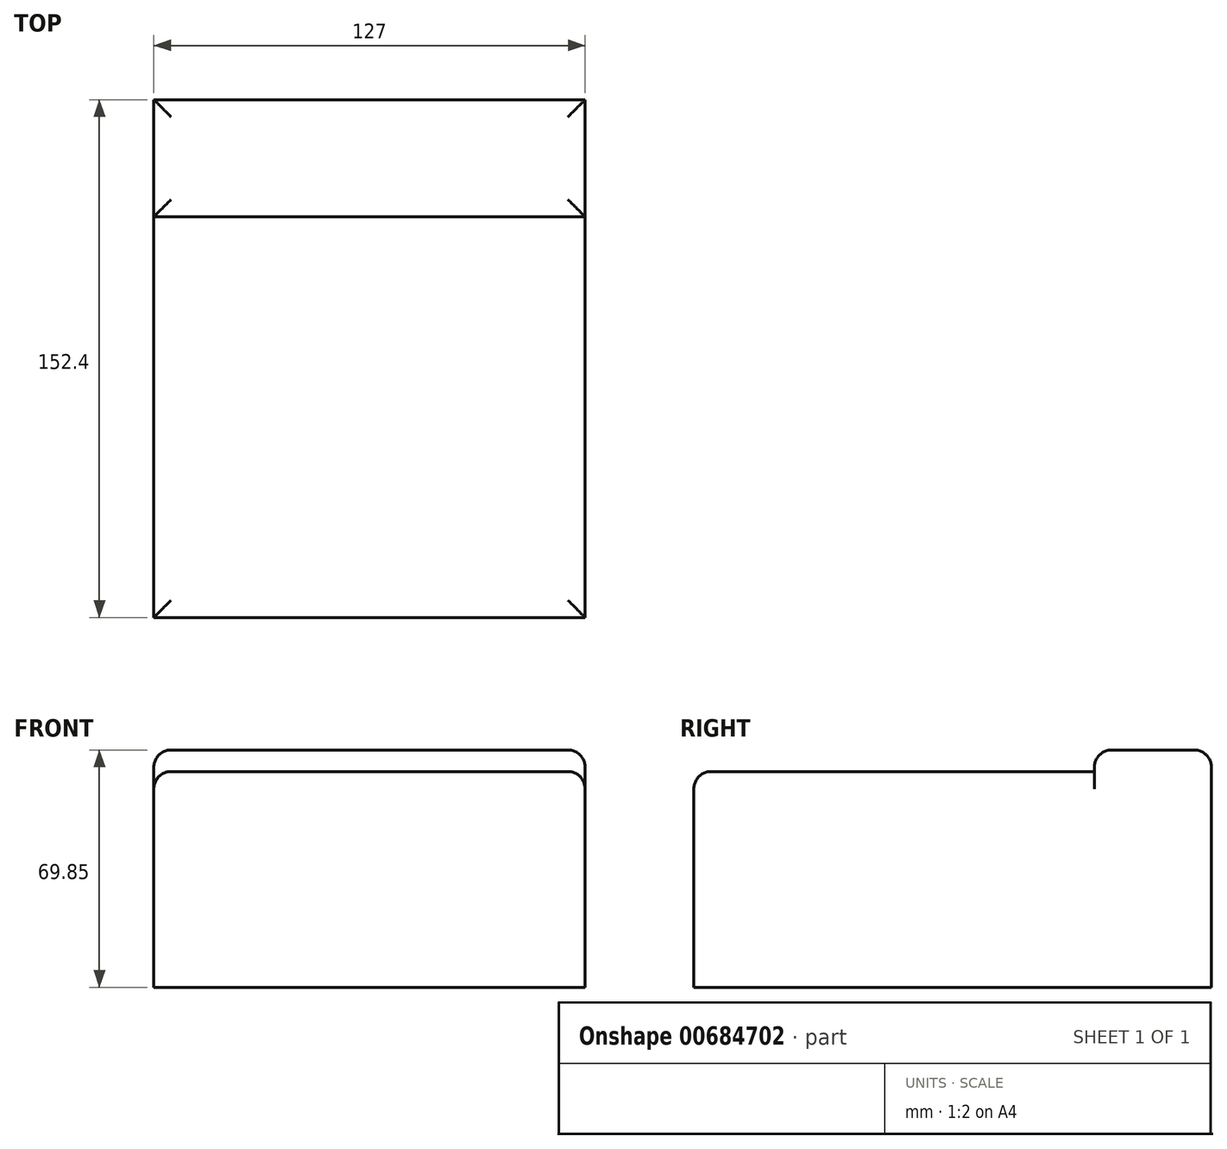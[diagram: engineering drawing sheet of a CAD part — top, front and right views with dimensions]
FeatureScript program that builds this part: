
annotation { "Feature Type Name" : "Feature", "Feature Type Description" : "" }
export const myFeature = defineFeature(function(context is Context, id is Id, definition is map)
    precondition{}
    {
        {
            var Q0;
            Q0=qCreatedBy(makeId("Top.planeOp"),FACE);
            var sketch = newSketch(context, id + "F0", { "sketchPlane" : qUnion([Q0])});
            skLineSegment(sketch, "E0.bottom", {"start": v(-73.34, 101.78) * mm, "end": v(53.66, 101.78) * mm});
            skLineSegment(sketch, "E0.top", {"start": v(-73.34, -50.62) * mm, "end": v(53.66, -50.62) * mm});
            skLineSegment(sketch, "E0.left", {"start": v(-73.34, 101.78) * mm, "end": v(-73.34, -50.62) * mm});
            skLineSegment(sketch, "E0.right", {"start": v(53.66, 101.78) * mm, "end": v(53.66, -50.62) * mm});
            skSolve(sketch);
        }
        {
            var Q0;
            Q0=qSketchRegion(id+"F0",true);
            extrude(context, id + "F1", {"entities" : qUnion([Q0]), "depth" : 63.5 * mm, "offsetDistance" : 25.4 * mm});
        }
        {
            var Q0;
            Q0=makeQuery(id+"F1.opExtrude","CAP_FACE",FACE,{"disambiguationData":[OSD([sQuery(id+"F0.wireOp",EDGE,"E0.bottom"),sQuery(id+"F0.wireOp",EDGE,"E0.top"),sQuery(id+"F0.wireOp",EDGE,"E0.left"),sQuery(id+"F0.wireOp",EDGE,"E0.right")])],"isStart":false});
            var sketch = newSketch(context, id + "F2", { "sketchPlane" : qUnion([Q0])});
            skLineSegment(sketch, "E1.bottom", {"start": v(-73.34, 101.78) * mm, "end": v(53.66, 101.78) * mm});
            skLineSegment(sketch, "E1.top", {"start": v(-73.34, 67.31) * mm, "end": v(53.66, 67.31) * mm});
            skLineSegment(sketch, "E1.left", {"start": v(-73.34, 101.78) * mm, "end": v(-73.34, 67.31) * mm});
            skLineSegment(sketch, "E1.right", {"start": v(53.66, 101.78) * mm, "end": v(53.66, 67.31) * mm});
            skSolve(sketch);
        }
        {
            var Q0;
            Q0=qSketchRegion(id+"F2",true);
            extrude(context, id + "F3", {"entities" : qUnion([Q0]), "operationType" : NewBodyOperationType.ADD, "depth" : 6.35 * mm, "offsetDistance" : 25.4 * mm});
        }
        {
            var Q0;
            Q0=makeQuery(id+"F3.opExtrude","CAP_EDGE",EDGE,{"disambiguationData":[OSD([sQuery(id+"F2.wireOp",EDGE,"E1.top")])],"isStart":false});
            var Q1;
            Q1=makeQuery(id+"F1.opExtrude","CAP_EDGE",EDGE,{"disambiguationData":[OSD([sQuery(id+"F0.wireOp",EDGE,"E0.right")])],"isStart":false});
            var Q2;
            Q2=makeQuery(id+"F1.opExtrude","CAP_EDGE",EDGE,{"disambiguationData":[OSD([sQuery(id+"F0.wireOp",EDGE,"E0.top")])],"isStart":false});
            var Q3;
            Q3=makeQuery(id+"F1.opExtrude","CAP_EDGE",EDGE,{"disambiguationData":[OSD([sQuery(id+"F0.wireOp",EDGE,"E0.left")])],"isStart":false});
            var Q4;
            Q4=makeQuery(id+"F3.opExtrude","CAP_EDGE",EDGE,{"disambiguationData":[OSD([sQuery(id+"F2.wireOp",EDGE,"E1.bottom")])],"isStart":false});
            var Q5;
            Q5=makeQuery(id+"F3.opExtrude","CAP_EDGE",EDGE,{"disambiguationData":[OSD([sQuery(id+"F2.wireOp",EDGE,"E1.right")])],"isStart":false});
            var Q6;
            Q6=makeQuery(id+"F3.opExtrude","CAP_EDGE",EDGE,{"disambiguationData":[OSD([sQuery(id+"F2.wireOp",EDGE,"E1.left")])],"isStart":false});
            fillet(context, id + "F4", {"entities" : qUnion([Q0, Q1, Q2, Q3, Q4, Q5, Q6]), "radius" : 5.08 * mm, "tangentPropagation" : true, "allowEdgeOverflow" : false});
        }
    });
